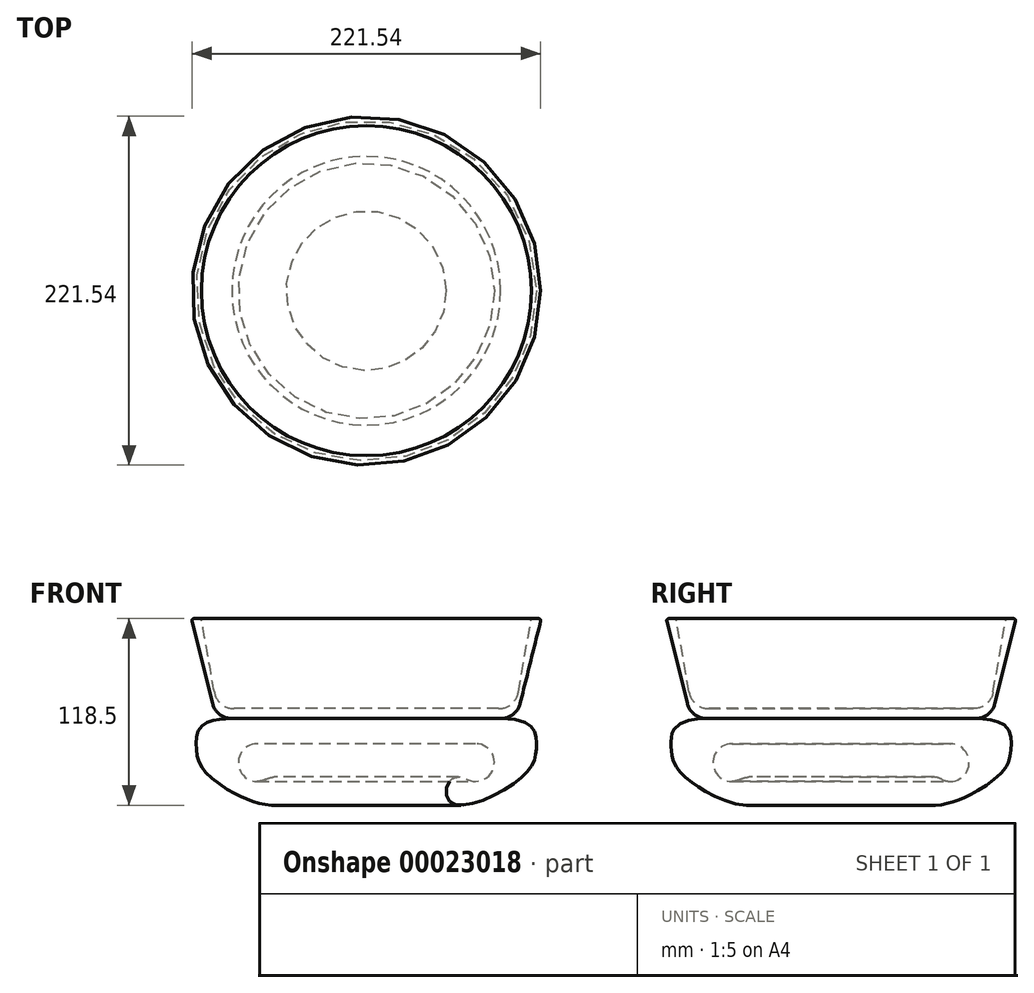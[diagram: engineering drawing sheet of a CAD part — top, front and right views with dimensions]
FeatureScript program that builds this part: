
annotation { "Feature Type Name" : "Feature", "Feature Type Description" : "" }
export const myFeature = defineFeature(function(context is Context, id is Id, definition is map)
    precondition{}
    {
        {
            var Q0;
            Q0=qCreatedBy(makeId("Top.planeOp"),FACE);
            var sketch = newSketch(context, id + "F0", { "sketchPlane" : qUnion([Q0])});
            skCircle(sketch, "E0", {"center": v(0, 0) * mm, "radius": 95.25 * mm});
            skSolve(sketch);
        }
        {
            var Q0;
            Q0=qCreatedBy(makeId("Top.planeOp"),FACE);
            cPlane(context, id + "F1", {"entities" : qUnion([Q0]), "cplaneType" : CPlaneType.OFFSET, "offset" : 63.5 * mm, "width" : 152.4 * mm, "height" : 152.4 * mm});
        }
        {
            var Q0;
            Q0=qCreatedBy(id+"F1.planeOp",FACE);
            var sketch = newSketch(context, id + "F2", { "sketchPlane" : qUnion([Q0])});
            skCircle(sketch, "E1", {"center": v(0, 0) * mm, "radius": 111.12 * mm});
            skSolve(sketch);
        }
        {
            var Q0;
            Q0 = qSketchRegion(id + "F0", true);
            var Q1;
            Q1 = qSketchRegion(id + "F2", true);
            loft(context, id + "F3", {"sheetProfilesArray" : [{ "sheetProfileEntities" : qUnion([Q0]) }, { "sheetProfileEntities" : qUnion([Q1]) }]});
        }
        {
            var Q0;
            Q0=makeQuery(id+"F3.opLoft","CAP_FACE",FACE,{"disambiguationData":[OSD([makeQuery(id+"F2.imprint","IMPRINT",FACE,{"disambiguationData":[TD([[makeQuery(id+"F2.imprint","IMPRINT",EDGE,{"derivedFrom":sQuery(id+"F2.wireOp",EDGE,"E1")}),1.0]])]})])],"isStart":true});
            var sketch = newSketch(context, id + "F4", { "sketchPlane" : qUnion([Q0])});
            skCircle(sketch, "E2", {"center": v(0, 0) * mm, "radius": 104.78 * mm});
            skSolve(sketch);
        }
        {
            var Q0;
            Q0 = qSketchRegion(id + "F4", true);
            extrude(context, id + "F5", {"entities" : qUnion([Q0]), "operationType" : NewBodyOperationType.REMOVE, "oppositeDirection" : true, "depth" : 57.15 * mm, "hasDraft" : true, "draftAngle" : 10 * degree, "draftPullDirection" : true});
        }
        {
            var Q0;
            Q0=makeQuery(id+"F5.boolean.opBoolean","COPY",EDGE,{"derivedFrom":makeQuery(id+"F5.opExtrude","CAP_EDGE",EDGE,{"disambiguationData":[OSD([sQuery(id+"F4.wireOp",EDGE,"E2")])],"isStart":false})});
            var Q1;
            Q1=makeQuery(id+"F3.opLoft","MID_CAP_EDGE",EDGE,{"disambiguationData":[OSD([sQuery(id+"F0.wireOp",EDGE,"E0")])],"capPos":0.0});
            fillet(context, id + "F6", {"entities" : qUnion([Q0, Q1]), "radius" : 12.7 * mm, "tangentPropagation" : true, "allowEdgeOverflow" : false});
        }
        {
            var Q0;
            Q0=makeQuery(id+"F3.opLoft","MID_CAP_EDGE",EDGE,{"disambiguationData":[OSD([sQuery(id+"F0.wireOp",EDGE,"E0"),sQuery(id+"F2.wireOp",EDGE,"E1")])],"capPos":1.0});
            var Q1;
            Q1=makeQuery(id+"F5.boolean.opBoolean","COPY",EDGE,{"derivedFrom":makeQuery(id+"F5.opExtrude","CAP_EDGE",EDGE,{"disambiguationData":[OSD([sQuery(id+"F4.wireOp",EDGE,"E2")])],"isStart":true})});
            fillet(context, id + "F7", {"entities" : qUnion([Q0, Q1]), "radius" : 1.27 * mm, "tangentPropagation" : true, "allowEdgeOverflow" : false});
        }
        {
            var Q0;
            Q0=qCreatedBy(makeId("Front.planeOp"),FACE);
            var sketch = newSketch(context, id + "F8", { "sketchPlane" : qUnion([Q0])});
            skLineSegment(sketch, "E3", {"start": v(0, 0) * mm, "end": v(-85.33, 0) * mm});
            skFitSpline(sketch, "E4", {"points": [v(-85.33, 0) * mm, v(-108.03, -16.68) * mm, v(-99.06, -37.15) * mm, v(-52.24, -51.88) * mm, v(-64.04, -38.63) * mm], "startDerivative": vector(-266.37, 0) * mm, "endDerivative": vector(-180.78, -89.97) * mm});
            skArc(sketch, "E5", {"start": v(-69.37, -15.97) * mm, "mid": v(-81, -30.66) * mm, "end": v(-64.04, -38.63) * mm});
            skLineSegment(sketch, "E6", {"start": v(-69.37, -15.97) * mm, "end": v(0, -15.97) * mm});
            skLineSegment(sketch, "E7", {"start": v(0, -15.97) * mm, "end": v(0, 0) * mm});
            skSolve(sketch);
        }
        {
            var Q0;
            Q0=qCreatedBy(makeId("Front.planeOp"),FACE);
            var sketch = newSketch(context, id + "F9", { "sketchPlane" : qUnion([Q0])});
            skLineSegment(sketch, "E8", {"start": v(0, 0) * mm, "end": v(0, -42.13) * mm, "construction": true});
            skSolve(sketch);
        }
        {
            var Q0;
            Q0 = qSketchRegion(id + "F8", true);
            var Q1;
            Q1=sQuery(id+"F9.wireOp",EDGE,"E8");
            revolve(context, id + "F10", {"operationType" : NewBodyOperationType.ADD, "entities" : qUnion([Q0]), "axis" : qUnion([Q1]), "revolveType" : RevolveType.FULL});
        }
    });
